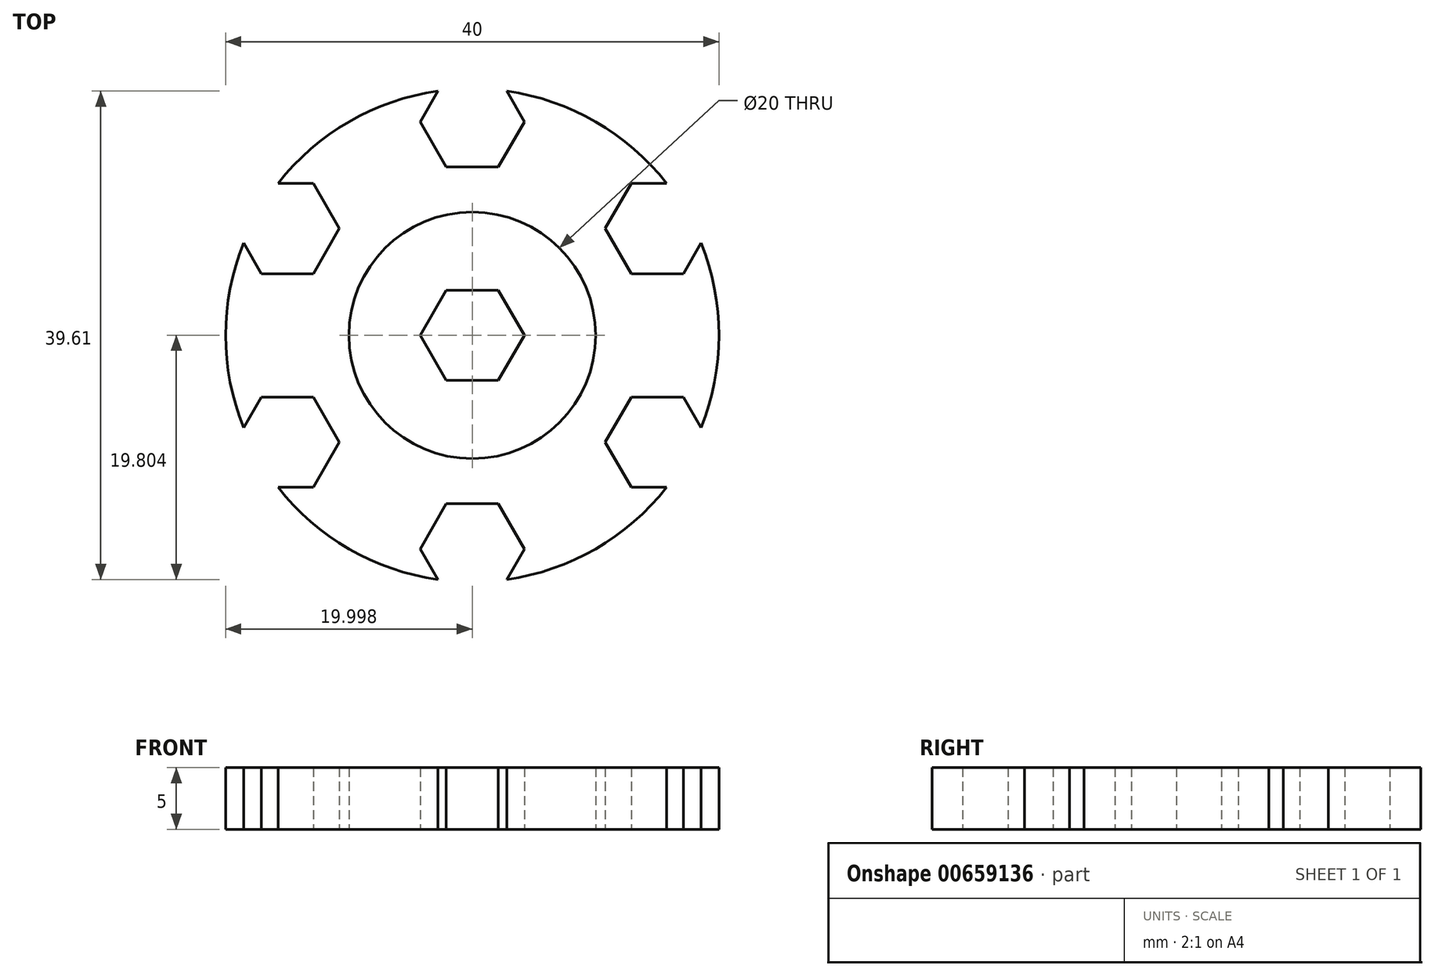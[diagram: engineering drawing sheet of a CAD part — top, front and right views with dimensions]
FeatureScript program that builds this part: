
annotation { "Feature Type Name" : "Feature", "Feature Type Description" : "" }
export const myFeature = defineFeature(function(context is Context, id is Id, definition is map)
    precondition{}
    {
        {
            var Q0;
            Q0=qCreatedBy(makeId("Top.planeOp"),FACE);
            var sketch = newSketch(context, id + "F0", { "sketchPlane" : qUnion([Q0])});
            skLineSegment(sketch, "E0.0", {"start": v(-11.35, 1.25) * mm, "end": v(-21.35, 1.25) * mm});
            skLineSegment(sketch, "E0.1", {"start": v(-21.35, 1.25) * mm, "end": v(-26.35, 9.91) * mm});
            skLineSegment(sketch, "E0.2", {"start": v(-26.35, 9.91) * mm, "end": v(-21.35, 18.57) * mm});
            skLineSegment(sketch, "E0.3", {"start": v(-21.35, 18.57) * mm, "end": v(-11.35, 18.57) * mm});
            skLineSegment(sketch, "E0.4", {"start": v(-11.35, 18.57) * mm, "end": v(-6.35, 9.91) * mm});
            skLineSegment(sketch, "E0.5", {"start": v(-6.35, 9.91) * mm, "end": v(-11.35, 1.25) * mm});
            skPoint(sketch, "E0.0.midPoint", {"position": v(-16.35, 1.25) * mm});
            skLineSegment(sketch, "E1", {"start": v(-21.35, 1.25) * mm, "end": v(-11.35, 1.25) * mm});
            skLineSegment(sketch, "E2", {"start": v(-11.35, 1.25) * mm, "end": v(-6.35, 9.91) * mm});
            skLineSegment(sketch, "E3", {"start": v(-6.35, 9.91) * mm, "end": v(-11.35, 18.57) * mm});
            skLineSegment(sketch, "E4", {"start": v(-11.35, 18.57) * mm, "end": v(-21.35, 18.57) * mm});
            skLineSegment(sketch, "E5", {"start": v(-21.35, 18.57) * mm, "end": v(-26.35, 9.91) * mm});
            skLineSegment(sketch, "E6", {"start": v(-26.35, 9.91) * mm, "end": v(-21.35, 1.25) * mm});
            skLineSegment(sketch, "E7.MirrorCS", {"start": v(-6.35, 27.23) * mm, "end": v(-11.35, 35.9) * mm});
            skLineSegment(sketch, "E8.MirrorCS", {"start": v(-21.35, 35.9) * mm, "end": v(-26.35, 27.23) * mm});
            skLineSegment(sketch, "E9.MirrorCS", {"start": v(-26.35, 27.23) * mm, "end": v(-21.35, 18.57) * mm});
            skLineSegment(sketch, "E10.MirrorCS", {"start": v(-11.35, 35.9) * mm, "end": v(-6.35, 27.23) * mm});
            skLineSegment(sketch, "E11.MirrorCS", {"start": v(-11.35, 35.9) * mm, "end": v(-21.35, 35.9) * mm});
            skLineSegment(sketch, "E12.MirrorCS", {"start": v(-11.35, 18.57) * mm, "end": v(-6.35, 27.23) * mm});
            skLineSegment(sketch, "E13.MirrorCS", {"start": v(-21.35, 35.9) * mm, "end": v(-11.35, 35.9) * mm});
            skLineSegment(sketch, "E14.MirrorCS", {"start": v(-6.35, 27.23) * mm, "end": v(-11.35, 18.57) * mm});
            skLineSegment(sketch, "E15.MirrorCS", {"start": v(-26.35, 27.23) * mm, "end": v(-21.35, 35.9) * mm});
            skLineSegment(sketch, "E16.MirrorCS", {"start": v(-21.35, 18.57) * mm, "end": v(-26.35, 27.23) * mm});
            skPoint(sketch, "E17.MirrorP", {"position": v(-16.35, 35.9) * mm});
            skLineSegment(sketch, "E18.MirrorCS", {"start": v(-6.35, 9.91) * mm, "end": v(3.65, 9.91) * mm});
            skLineSegment(sketch, "E19.MirrorCS", {"start": v(3.65, 9.91) * mm, "end": v(8.65, 18.57) * mm});
            skLineSegment(sketch, "E20.MirrorCS", {"start": v(8.65, 18.57) * mm, "end": v(3.65, 27.23) * mm});
            skLineSegment(sketch, "E21.MirrorCS", {"start": v(3.65, 27.23) * mm, "end": v(-6.35, 27.23) * mm});
            skLineSegment(sketch, "E22.MirrorCS", {"start": v(3.65, 9.91) * mm, "end": v(-6.35, 9.91) * mm});
            skPoint(sketch, "E23.MirrorP", {"position": v(6.15, 14.24) * mm});
            skLineSegment(sketch, "E24.MirrorCS", {"start": v(-6.35, 27.23) * mm, "end": v(3.65, 27.23) * mm});
            skLineSegment(sketch, "E25.MirrorCS", {"start": v(8.65, 18.57) * mm, "end": v(3.65, 9.91) * mm});
            skLineSegment(sketch, "E26.MirrorCS", {"start": v(3.65, 27.23) * mm, "end": v(8.65, 18.57) * mm});
            skLineSegment(sketch, "E27.MirrorCS", {"start": v(8.65, 1.25) * mm, "end": v(3.65, 9.91) * mm});
            skLineSegment(sketch, "E28.MirrorCS", {"start": v(3.65, -7.4) * mm, "end": v(8.65, 1.25) * mm});
            skLineSegment(sketch, "E29.MirrorCS", {"start": v(-6.35, -7.4) * mm, "end": v(3.65, -7.4) * mm});
            skLineSegment(sketch, "E30.MirrorCS", {"start": v(-11.35, 1.25) * mm, "end": v(-6.35, -7.4) * mm});
            skLineSegment(sketch, "E31.MirrorCS", {"start": v(3.65, 9.91) * mm, "end": v(8.65, 1.25) * mm});
            skPoint(sketch, "E32.MirrorP", {"position": v(-8.85, -3.08) * mm});
            skLineSegment(sketch, "E33.MirrorCS", {"start": v(3.65, -7.4) * mm, "end": v(-6.35, -7.4) * mm});
            skLineSegment(sketch, "E34.MirrorCS", {"start": v(-6.35, -7.4) * mm, "end": v(-11.35, 1.25) * mm});
            skLineSegment(sketch, "E35.MirrorCS", {"start": v(8.65, 1.25) * mm, "end": v(3.65, -7.4) * mm});
            skLineSegment(sketch, "E36.MirrorCS", {"start": v(-11.35, -16.07) * mm, "end": v(-6.35, -7.4) * mm});
            skLineSegment(sketch, "E37.MirrorCS", {"start": v(-6.35, -7.4) * mm, "end": v(-11.35, -16.07) * mm});
            skLineSegment(sketch, "E38.MirrorCS", {"start": v(-21.35, -16.07) * mm, "end": v(-11.35, -16.07) * mm});
            skLineSegment(sketch, "E39.MirrorCS", {"start": v(-21.35, 1.25) * mm, "end": v(-26.35, -7.4) * mm});
            skLineSegment(sketch, "E40.MirrorCS", {"start": v(-26.35, -7.4) * mm, "end": v(-21.35, -16.07) * mm});
            skLineSegment(sketch, "E41.MirrorCS", {"start": v(-11.35, -16.07) * mm, "end": v(-21.35, -16.07) * mm});
            skLineSegment(sketch, "E42.MirrorCS", {"start": v(-26.35, -7.4) * mm, "end": v(-21.35, 1.25) * mm});
            skLineSegment(sketch, "E43.MirrorCS", {"start": v(-21.35, -16.07) * mm, "end": v(-26.35, -7.4) * mm});
            skLineSegment(sketch, "E44.MirrorCS", {"start": v(-36.35, -7.4) * mm, "end": v(-26.35, -7.4) * mm});
            skLineSegment(sketch, "E45.MirrorCS", {"start": v(-41.35, 1.25) * mm, "end": v(-36.35, -7.4) * mm});
            skLineSegment(sketch, "E46.MirrorCS", {"start": v(-36.35, -7.4) * mm, "end": v(-41.35, 1.25) * mm});
            skLineSegment(sketch, "E47.MirrorCS", {"start": v(-26.35, -7.4) * mm, "end": v(-36.35, -7.4) * mm});
            skLineSegment(sketch, "E48.MirrorCS", {"start": v(-36.35, 9.91) * mm, "end": v(-41.35, 1.25) * mm});
            skLineSegment(sketch, "E49.MirrorCS", {"start": v(-41.35, 1.25) * mm, "end": v(-36.35, 9.91) * mm});
            skLineSegment(sketch, "E50.MirrorCS", {"start": v(-26.35, 9.91) * mm, "end": v(-36.35, 9.91) * mm});
            skLineSegment(sketch, "E51.MirrorCS", {"start": v(-36.35, 9.91) * mm, "end": v(-26.35, 9.91) * mm});
            skLineSegment(sketch, "E52.MirrorCS", {"start": v(-26.35, 27.23) * mm, "end": v(-36.35, 27.23) * mm});
            skLineSegment(sketch, "E53.MirrorCS", {"start": v(-36.35, 27.23) * mm, "end": v(-41.35, 18.57) * mm});
            skLineSegment(sketch, "E54.MirrorCS", {"start": v(-41.35, 18.57) * mm, "end": v(-36.35, 9.91) * mm});
            skLineSegment(sketch, "E55.MirrorCS", {"start": v(-41.35, 18.57) * mm, "end": v(-36.35, 27.23) * mm});
            skLineSegment(sketch, "E56.MirrorCS", {"start": v(-36.35, 27.23) * mm, "end": v(-26.35, 27.23) * mm});
            skPoint(sketch, "E57.MirrorP", {"position": v(-38.85, 14.24) * mm});
            skLineSegment(sketch, "E58.MirrorCS", {"start": v(-36.35, 9.91) * mm, "end": v(-41.35, 18.57) * mm});
            skLineSegment(sketch, "E59.MirrorCS", {"start": v(-26.35, 44.55) * mm, "end": v(-36.35, 44.55) * mm});
            skLineSegment(sketch, "E60.MirrorCS", {"start": v(-41.35, 35.9) * mm, "end": v(-36.35, 27.23) * mm});
            skLineSegment(sketch, "E61.MirrorCS", {"start": v(-36.35, 44.55) * mm, "end": v(-26.35, 44.55) * mm});
            skLineSegment(sketch, "E62.MirrorCS", {"start": v(-26.35, 44.55) * mm, "end": v(-21.35, 35.9) * mm});
            skLineSegment(sketch, "E63.MirrorCS", {"start": v(-36.35, 44.55) * mm, "end": v(-41.35, 35.9) * mm});
            skLineSegment(sketch, "E64.MirrorCS", {"start": v(-36.35, 27.23) * mm, "end": v(-41.35, 35.9) * mm});
            skLineSegment(sketch, "E65.MirrorCS", {"start": v(-21.35, 35.9) * mm, "end": v(-26.35, 44.55) * mm});
            skPoint(sketch, "E66.MirrorP", {"position": v(-38.85, 40.22) * mm});
            skLineSegment(sketch, "E67.MirrorCS", {"start": v(-41.35, 35.9) * mm, "end": v(-36.35, 44.55) * mm});
            skLineSegment(sketch, "E68.MirrorCS", {"start": v(-56.35, 9.91) * mm, "end": v(-51.35, 18.57) * mm});
            skLineSegment(sketch, "E69.MirrorCS", {"start": v(-41.35, 1.25) * mm, "end": v(-51.35, 1.25) * mm});
            skLineSegment(sketch, "E70.MirrorCS", {"start": v(-56.35, 9.91) * mm, "end": v(-51.35, 1.25) * mm});
            skLineSegment(sketch, "E71.MirrorCS", {"start": v(-51.35, 1.25) * mm, "end": v(-56.35, 9.91) * mm});
            skLineSegment(sketch, "E72.MirrorCS", {"start": v(-51.35, 18.57) * mm, "end": v(-56.35, 9.91) * mm});
            skLineSegment(sketch, "E73.MirrorCS", {"start": v(-51.35, 18.57) * mm, "end": v(-41.35, 18.57) * mm});
            skLineSegment(sketch, "E74.MirrorCS", {"start": v(-41.35, 18.57) * mm, "end": v(-51.35, 18.57) * mm});
            skLineSegment(sketch, "E75.MirrorCS", {"start": v(-51.35, 1.25) * mm, "end": v(-41.35, 1.25) * mm});
            skLineSegment(sketch, "E76.MirrorCS", {"start": v(-6.35, 44.55) * mm, "end": v(3.65, 44.55) * mm});
            skLineSegment(sketch, "E77.MirrorCS", {"start": v(3.65, 44.55) * mm, "end": v(-6.35, 44.55) * mm});
            skLineSegment(sketch, "E78.MirrorCS", {"start": v(8.65, 35.9) * mm, "end": v(3.65, 44.55) * mm});
            skLineSegment(sketch, "E79.MirrorCS", {"start": v(3.65, 44.55) * mm, "end": v(8.65, 35.9) * mm});
            skLineSegment(sketch, "E80.MirrorCS", {"start": v(8.65, 35.9) * mm, "end": v(3.65, 27.23) * mm});
            skLineSegment(sketch, "E81.MirrorCS", {"start": v(3.65, 27.23) * mm, "end": v(8.65, 35.9) * mm});
            skLineSegment(sketch, "E82.MirrorCS", {"start": v(-6.35, 44.55) * mm, "end": v(-11.35, 35.9) * mm});
            skLineSegment(sketch, "E83.MirrorCS", {"start": v(-11.35, 35.9) * mm, "end": v(-6.35, 44.55) * mm});
            skPoint(sketch, "E84.MirrorP", {"position": v(-8.85, 40.22) * mm});
            skLineSegment(sketch, "E85.MirrorCS", {"start": v(23.65, 9.91) * mm, "end": v(18.65, 18.57) * mm});
            skLineSegment(sketch, "E86.MirrorCS", {"start": v(18.65, 1.25) * mm, "end": v(23.65, 9.91) * mm});
            skLineSegment(sketch, "E87.MirrorCS", {"start": v(18.65, 18.57) * mm, "end": v(23.65, 9.91) * mm});
            skLineSegment(sketch, "E88.MirrorCS", {"start": v(23.65, 9.91) * mm, "end": v(18.65, 1.25) * mm});
            skLineSegment(sketch, "E89.MirrorCS", {"start": v(18.65, 1.25) * mm, "end": v(8.65, 1.25) * mm});
            skLineSegment(sketch, "E90.MirrorCS", {"start": v(18.65, 18.57) * mm, "end": v(8.65, 18.57) * mm});
            skLineSegment(sketch, "E91.MirrorCS", {"start": v(8.65, 1.25) * mm, "end": v(18.65, 1.25) * mm});
            skLineSegment(sketch, "E92.MirrorCS", {"start": v(8.65, 18.57) * mm, "end": v(18.65, 18.57) * mm});
            skLineSegment(sketch, "E93.MirrorCS", {"start": v(8.65, -16.07) * mm, "end": v(3.65, -24.73) * mm});
            skLineSegment(sketch, "E94.MirrorCS", {"start": v(3.65, -24.73) * mm, "end": v(8.65, -16.07) * mm});
            skLineSegment(sketch, "E95.MirrorCS", {"start": v(3.65, -24.73) * mm, "end": v(-6.35, -24.73) * mm});
            skLineSegment(sketch, "E96.MirrorCS", {"start": v(-6.35, -24.73) * mm, "end": v(3.65, -24.73) * mm});
            skLineSegment(sketch, "E97.MirrorCS", {"start": v(-6.35, -24.73) * mm, "end": v(-11.35, -16.07) * mm});
            skLineSegment(sketch, "E98.MirrorCS", {"start": v(-11.35, -16.07) * mm, "end": v(-6.35, -24.73) * mm});
            skPoint(sketch, "E99.MirrorP", {"position": v(-16.35, -16.07) * mm});
            skLineSegment(sketch, "E100.MirrorCS", {"start": v(8.65, -16.07) * mm, "end": v(3.65, -7.4) * mm});
            skPoint(sketch, "E101.MirrorP", {"position": v(-8.85, -11.74) * mm});
            skLineSegment(sketch, "E102.MirrorCS", {"start": v(3.65, -7.4) * mm, "end": v(8.65, -16.07) * mm});
            skLineSegment(sketch, "E103.MirrorCS", {"start": v(-26.35, -24.73) * mm, "end": v(-36.35, -24.73) * mm});
            skLineSegment(sketch, "E104.MirrorCS", {"start": v(-36.35, -24.73) * mm, "end": v(-26.35, -24.73) * mm});
            skLineSegment(sketch, "E105.MirrorCS", {"start": v(-36.35, -24.73) * mm, "end": v(-41.35, -16.07) * mm});
            skLineSegment(sketch, "E106.MirrorCS", {"start": v(-41.35, -16.07) * mm, "end": v(-36.35, -24.73) * mm});
            skLineSegment(sketch, "E107.MirrorCS", {"start": v(-41.35, -16.07) * mm, "end": v(-36.35, -7.4) * mm});
            skLineSegment(sketch, "E108.MirrorCS", {"start": v(-26.35, -24.73) * mm, "end": v(-21.35, -16.07) * mm});
            skPoint(sketch, "E109.MirrorP", {"position": v(-38.85, -11.74) * mm});
            skLineSegment(sketch, "E110.MirrorCS", {"start": v(-21.35, -16.07) * mm, "end": v(-26.35, -24.73) * mm});
            skPoint(sketch, "E111.MirrorP", {"position": v(-23.85, -20.4) * mm});
            skLineSegment(sketch, "E112.MirrorCS", {"start": v(-36.35, -7.4) * mm, "end": v(-41.35, -16.07) * mm});
            skPoint(sketch, "E113.MirrorP", {"position": v(-38.85, -20.4) * mm});
            skPoint(sketch, "E114.MirrorP", {"position": v(-31.35, -24.73) * mm});
            skLineSegment(sketch, "E115.0", {"start": v(107.66, 12.57) * mm, "end": v(97.66, 12.57) * mm});
            skLineSegment(sketch, "E115.1", {"start": v(97.66, 12.57) * mm, "end": v(91.43, 20.38) * mm});
            skLineSegment(sketch, "E115.2", {"start": v(91.43, 20.38) * mm, "end": v(93.66, 30.13) * mm});
            skLineSegment(sketch, "E115.3", {"start": v(93.66, 30.13) * mm, "end": v(102.66, 34.47) * mm});
            skLineSegment(sketch, "E115.4", {"start": v(102.66, 34.47) * mm, "end": v(111.67, 30.13) * mm});
            skLineSegment(sketch, "E115.5", {"start": v(111.67, 30.13) * mm, "end": v(113.9, 20.38) * mm});
            skLineSegment(sketch, "E115.6", {"start": v(113.9, 20.38) * mm, "end": v(107.66, 12.57) * mm});
            skPoint(sketch, "E115.0.midPoint", {"position": v(102.66, 12.57) * mm});
            skLineSegment(sketch, "E116", {"start": v(97.66, 12.57) * mm, "end": v(107.66, 12.57) * mm});
            skLineSegment(sketch, "E117", {"start": v(107.66, 12.57) * mm, "end": v(113.9, 20.38) * mm});
            skLineSegment(sketch, "E118", {"start": v(113.9, 20.38) * mm, "end": v(111.67, 30.13) * mm});
            skLineSegment(sketch, "E119", {"start": v(111.67, 30.13) * mm, "end": v(102.66, 34.47) * mm});
            skLineSegment(sketch, "E120", {"start": v(102.66, 34.47) * mm, "end": v(93.66, 30.13) * mm});
            skLineSegment(sketch, "E121", {"start": v(93.66, 30.13) * mm, "end": v(91.43, 20.38) * mm});
            skLineSegment(sketch, "E122", {"start": v(91.43, 20.38) * mm, "end": v(97.66, 12.57) * mm});
            skLineSegment(sketch, "E123.MirrorCS", {"start": v(106.67, 52.04) * mm, "end": v(116.67, 52.04) * mm});
            skLineSegment(sketch, "E124.MirrorCS", {"start": v(100.44, 44.22) * mm, "end": v(106.67, 52.04) * mm});
            skLineSegment(sketch, "E125.MirrorCS", {"start": v(116.67, 52.04) * mm, "end": v(122.9, 44.22) * mm});
            skLineSegment(sketch, "E126.MirrorCS", {"start": v(120.68, 34.47) * mm, "end": v(111.67, 30.13) * mm});
            skLineSegment(sketch, "E127.MirrorCS", {"start": v(122.9, 44.22) * mm, "end": v(120.68, 34.47) * mm});
            skLineSegment(sketch, "E128.MirrorCS", {"start": v(102.66, 34.47) * mm, "end": v(100.44, 44.22) * mm});
            skLineSegment(sketch, "E129.MirrorCS", {"start": v(116.67, 52.04) * mm, "end": v(106.67, 52.04) * mm});
            skLineSegment(sketch, "E130.MirrorCS", {"start": v(106.67, 52.04) * mm, "end": v(100.44, 44.22) * mm});
            skLineSegment(sketch, "E131.MirrorCS", {"start": v(100.44, 44.22) * mm, "end": v(102.66, 34.47) * mm});
            skLineSegment(sketch, "E132.MirrorCS", {"start": v(111.67, 30.13) * mm, "end": v(120.68, 34.47) * mm});
            skLineSegment(sketch, "E133.MirrorCS", {"start": v(122.9, 44.22) * mm, "end": v(116.67, 52.04) * mm});
            skLineSegment(sketch, "E134.MirrorCS", {"start": v(120.68, 34.47) * mm, "end": v(122.9, 44.22) * mm});
            skPoint(sketch, "E135.MirrorP", {"position": v(119.8, 48.13) * mm});
            skLineSegment(sketch, "E136.MirrorCS", {"start": v(111.67, 30.13) * mm, "end": v(117.9, 37.95) * mm});
            skLineSegment(sketch, "E137.MirrorCS", {"start": v(131.92, 20.38) * mm, "end": v(122.9, 16.05) * mm});
            skLineSegment(sketch, "E138.MirrorCS", {"start": v(134.14, 30.13) * mm, "end": v(131.92, 20.38) * mm});
            skLineSegment(sketch, "E139.MirrorCS", {"start": v(127.9, 37.95) * mm, "end": v(134.14, 30.13) * mm});
            skLineSegment(sketch, "E140.MirrorCS", {"start": v(122.9, 16.05) * mm, "end": v(113.9, 20.38) * mm});
            skLineSegment(sketch, "E141.MirrorCS", {"start": v(117.9, 37.95) * mm, "end": v(127.9, 37.95) * mm});
            skLineSegment(sketch, "E142.MirrorCS", {"start": v(131.92, 20.38) * mm, "end": v(134.14, 30.13) * mm});
            skLineSegment(sketch, "E143.MirrorCS", {"start": v(134.14, 30.13) * mm, "end": v(127.9, 37.95) * mm});
            skLineSegment(sketch, "E144.MirrorCS", {"start": v(127.9, 37.95) * mm, "end": v(117.9, 37.95) * mm});
            skPoint(sketch, "E145.MirrorP", {"position": v(127.41, 18.21) * mm});
            skLineSegment(sketch, "E146.MirrorCS", {"start": v(117.9, 37.95) * mm, "end": v(111.67, 30.13) * mm});
            skLineSegment(sketch, "E147.MirrorCS", {"start": v(113.9, 20.38) * mm, "end": v(122.9, 16.05) * mm});
            skLineSegment(sketch, "E148.MirrorCS", {"start": v(122.9, 16.05) * mm, "end": v(131.92, 20.38) * mm});
            skLineSegment(sketch, "E149.MirrorCS", {"start": v(123.9, 20.38) * mm, "end": v(130.13, 12.57) * mm});
            skLineSegment(sketch, "E150.MirrorCS", {"start": v(113.9, 20.38) * mm, "end": v(123.9, 20.38) * mm});
            skLineSegment(sketch, "E151.MirrorCS", {"start": v(127.9, 2.82) * mm, "end": v(118.9, -1.52) * mm});
            skLineSegment(sketch, "E152.MirrorCS", {"start": v(130.13, 12.57) * mm, "end": v(127.9, 2.82) * mm});
            skLineSegment(sketch, "E153.MirrorCS", {"start": v(109.89, 2.82) * mm, "end": v(107.66, 12.57) * mm});
            skLineSegment(sketch, "E154.MirrorCS", {"start": v(118.9, -1.52) * mm, "end": v(109.89, 2.82) * mm});
            skLineSegment(sketch, "E155.MirrorCS", {"start": v(107.66, 12.57) * mm, "end": v(109.89, 2.82) * mm});
            skPoint(sketch, "E156.MirrorP", {"position": v(108.78, 7.7) * mm});
            skLineSegment(sketch, "E157.MirrorCS", {"start": v(123.9, 20.38) * mm, "end": v(113.9, 20.38) * mm});
            skLineSegment(sketch, "E158.MirrorCS", {"start": v(127.9, 2.82) * mm, "end": v(130.13, 12.57) * mm});
            skLineSegment(sketch, "E159.MirrorCS", {"start": v(109.89, 2.82) * mm, "end": v(118.9, -1.52) * mm});
            skLineSegment(sketch, "E160.MirrorCS", {"start": v(130.13, 12.57) * mm, "end": v(123.9, 20.38) * mm});
            skLineSegment(sketch, "E161.MirrorCS", {"start": v(118.9, -1.52) * mm, "end": v(127.9, 2.82) * mm});
            skLineSegment(sketch, "E162.MirrorCS", {"start": v(107.66, 12.57) * mm, "end": v(113.9, 4.75) * mm});
            skLineSegment(sketch, "E163.MirrorCS", {"start": v(111.67, -5) * mm, "end": v(102.66, -9.34) * mm});
            skLineSegment(sketch, "E164.MirrorCS", {"start": v(113.9, 4.75) * mm, "end": v(111.67, -5) * mm});
            skLineSegment(sketch, "E165.MirrorCS", {"start": v(91.43, 4.75) * mm, "end": v(97.66, 12.57) * mm});
            skLineSegment(sketch, "E166.MirrorCS", {"start": v(93.66, -5) * mm, "end": v(91.43, 4.75) * mm});
            skLineSegment(sketch, "E167.MirrorCS", {"start": v(102.66, -9.34) * mm, "end": v(93.66, -5) * mm});
            skLineSegment(sketch, "E168.MirrorCS", {"start": v(97.66, 12.57) * mm, "end": v(91.43, 4.75) * mm});
            skLineSegment(sketch, "E169.MirrorCS", {"start": v(91.43, 4.75) * mm, "end": v(93.66, -5) * mm});
            skLineSegment(sketch, "E170.MirrorCS", {"start": v(93.66, -5) * mm, "end": v(102.66, -9.34) * mm});
            skLineSegment(sketch, "E171.MirrorCS", {"start": v(102.66, -9.34) * mm, "end": v(111.67, -5) * mm});
            skLineSegment(sketch, "E172.MirrorCS", {"start": v(111.67, -5) * mm, "end": v(113.9, 4.75) * mm});
            skLineSegment(sketch, "E173.MirrorCS", {"start": v(113.9, 4.75) * mm, "end": v(107.66, 12.57) * mm});
            skLineSegment(sketch, "E174.MirrorCS", {"start": v(97.66, 12.57) * mm, "end": v(95.44, 2.82) * mm});
            skLineSegment(sketch, "E175.MirrorCS", {"start": v(77.42, 2.82) * mm, "end": v(75.2, 12.57) * mm});
            skLineSegment(sketch, "E176.MirrorCS", {"start": v(86.43, -1.52) * mm, "end": v(77.42, 2.82) * mm});
            skLineSegment(sketch, "E177.MirrorCS", {"start": v(95.44, 2.82) * mm, "end": v(86.43, -1.52) * mm});
            skLineSegment(sketch, "E178.MirrorCS", {"start": v(81.43, 20.38) * mm, "end": v(91.43, 20.38) * mm});
            skLineSegment(sketch, "E179.MirrorCS", {"start": v(75.2, 12.57) * mm, "end": v(81.43, 20.38) * mm});
            skPoint(sketch, "E180.MirrorP", {"position": v(96.55, 7.7) * mm});
            skLineSegment(sketch, "E181.MirrorCS", {"start": v(86.43, -1.52) * mm, "end": v(95.44, 2.82) * mm});
            skLineSegment(sketch, "E182.MirrorCS", {"start": v(77.42, 2.82) * mm, "end": v(86.43, -1.52) * mm});
            skLineSegment(sketch, "E183.MirrorCS", {"start": v(95.44, 2.82) * mm, "end": v(97.66, 12.57) * mm});
            skLineSegment(sketch, "E184.MirrorCS", {"start": v(75.2, 12.57) * mm, "end": v(77.42, 2.82) * mm});
            skLineSegment(sketch, "E185.MirrorCS", {"start": v(81.43, 20.38) * mm, "end": v(75.2, 12.57) * mm});
            skLineSegment(sketch, "E186.MirrorCS", {"start": v(91.43, 20.38) * mm, "end": v(81.43, 20.38) * mm});
            skLineSegment(sketch, "E187.MirrorCS", {"start": v(82.42, 44.22) * mm, "end": v(88.66, 52.04) * mm});
            skLineSegment(sketch, "E188.MirrorCS", {"start": v(88.66, 52.04) * mm, "end": v(98.66, 52.04) * mm});
            skLineSegment(sketch, "E189.MirrorCS", {"start": v(84.65, 34.47) * mm, "end": v(82.42, 44.22) * mm});
            skLineSegment(sketch, "E190.MirrorCS", {"start": v(104.89, 44.22) * mm, "end": v(102.66, 34.47) * mm});
            skLineSegment(sketch, "E191.MirrorCS", {"start": v(98.66, 52.04) * mm, "end": v(104.89, 44.22) * mm});
            skLineSegment(sketch, "E192.MirrorCS", {"start": v(82.42, 44.22) * mm, "end": v(84.65, 34.47) * mm});
            skPoint(sketch, "E193.MirrorP", {"position": v(85.54, 48.13) * mm});
            skLineSegment(sketch, "E194.MirrorCS", {"start": v(93.66, 30.13) * mm, "end": v(84.65, 34.47) * mm});
            skLineSegment(sketch, "E195.MirrorCS", {"start": v(98.66, 52.04) * mm, "end": v(88.66, 52.04) * mm});
            skLineSegment(sketch, "E196.MirrorCS", {"start": v(84.65, 34.47) * mm, "end": v(93.66, 30.13) * mm});
            skLineSegment(sketch, "E197.MirrorCS", {"start": v(104.89, 44.22) * mm, "end": v(98.66, 52.04) * mm});
            skLineSegment(sketch, "E198.MirrorCS", {"start": v(102.66, 34.47) * mm, "end": v(104.89, 44.22) * mm});
            skLineSegment(sketch, "E199.MirrorCS", {"start": v(88.66, 52.04) * mm, "end": v(82.42, 44.22) * mm});
            skLineSegment(sketch, "E200.MirrorCS", {"start": v(82.42, 16.05) * mm, "end": v(73.41, 20.38) * mm});
            skLineSegment(sketch, "E201.MirrorCS", {"start": v(73.41, 20.38) * mm, "end": v(82.42, 16.05) * mm});
            skLineSegment(sketch, "E202.MirrorCS", {"start": v(87.42, 37.95) * mm, "end": v(93.66, 30.13) * mm});
            skLineSegment(sketch, "E203.MirrorCS", {"start": v(77.42, 37.95) * mm, "end": v(87.42, 37.95) * mm});
            skLineSegment(sketch, "E204.MirrorCS", {"start": v(71.19, 30.13) * mm, "end": v(77.42, 37.95) * mm});
            skLineSegment(sketch, "E205.MirrorCS", {"start": v(73.41, 20.38) * mm, "end": v(71.19, 30.13) * mm});
            skLineSegment(sketch, "E206.MirrorCS", {"start": v(91.43, 20.38) * mm, "end": v(82.42, 16.05) * mm});
            skLineSegment(sketch, "E207.MirrorCS", {"start": v(82.42, 16.05) * mm, "end": v(91.43, 20.38) * mm});
            skPoint(sketch, "E208.MirrorP", {"position": v(77.92, 18.21) * mm});
            skLineSegment(sketch, "E209.MirrorCS", {"start": v(93.66, 30.13) * mm, "end": v(87.42, 37.95) * mm});
            skLineSegment(sketch, "E210.MirrorCS", {"start": v(71.19, 30.13) * mm, "end": v(73.41, 20.38) * mm});
            skLineSegment(sketch, "E211.MirrorCS", {"start": v(77.42, 37.95) * mm, "end": v(71.19, 30.13) * mm});
            skLineSegment(sketch, "E212.MirrorCS", {"start": v(87.42, 37.95) * mm, "end": v(77.42, 37.95) * mm});
            skCircle(sketch, "E213", {"center": v(67.92, -62.3) * mm, "radius": 40 * mm});
            skLineSegment(sketch, "E214", {"start": v(-11.35, 18.57) * mm, "end": v(-21.35, 1.25) * mm});
            skLineSegment(sketch, "E215", {"start": v(-26.35, 9.91) * mm, "end": v(-6.35, 9.91) * mm});
            skLineSegment(sketch, "E216", {"start": v(-11.35, 1.25) * mm, "end": v(-21.35, 18.57) * mm});
            skPoint(sketch, "E217", {"position": v(-16.35, 9.91) * mm});
            skCircle(sketch, "E218", {"center": v(-16.35, 9.91) * mm, "radius": 15 * mm});
            skPoint(sketch, "E219", {"position": v(-31.35, 9.91) * mm});
            skPoint(sketch, "E220", {"position": v(-1.35, 9.91) * mm});
            skPoint(sketch, "E221", {"position": v(-23.85, -3.08) * mm});
            skPoint(sketch, "E222", {"position": v(-23.85, 22.9) * mm});
            skPoint(sketch, "E223", {"position": v(-8.85, 22.9) * mm});
            skLineSegment(sketch, "E224.0", {"start": v(-3.47, 39.55) * mm, "end": v(0.76, 39.55) * mm});
            skLineSegment(sketch, "E224.1", {"start": v(2.87, 35.9) * mm, "end": v(0.76, 32.23) * mm});
            skLineSegment(sketch, "E224.2", {"start": v(0.76, 32.23) * mm, "end": v(-3.47, 32.23) * mm});
            skLineSegment(sketch, "E224.3", {"start": v(0.76, 39.55) * mm, "end": v(2.87, 35.9) * mm});
            skLineSegment(sketch, "E224.4", {"start": v(-3.47, 32.23) * mm, "end": v(-5.58, 35.9) * mm});
            skLineSegment(sketch, "E224.5", {"start": v(-5.58, 35.9) * mm, "end": v(-3.47, 39.55) * mm});
            skLineSegment(sketch, "E225.0", {"start": v(0.76, 22.23) * mm, "end": v(-3.47, 22.23) * mm});
            skLineSegment(sketch, "E225.1", {"start": v(2.87, 18.57) * mm, "end": v(0.76, 14.91) * mm});
            skLineSegment(sketch, "E225.2", {"start": v(-3.47, 14.91) * mm, "end": v(0.76, 14.91) * mm});
            skLineSegment(sketch, "E225.3", {"start": v(0.76, 22.23) * mm, "end": v(2.87, 18.57) * mm});
            skLineSegment(sketch, "E225.4", {"start": v(-3.47, 14.91) * mm, "end": v(-5.58, 18.57) * mm});
            skLineSegment(sketch, "E225.5", {"start": v(-5.58, 18.57) * mm, "end": v(-3.47, 22.23) * mm});
            skLineSegment(sketch, "E226.0", {"start": v(-18.47, 30.9) * mm, "end": v(-20.58, 27.23) * mm});
            skLineSegment(sketch, "E226.1", {"start": v(-12.13, 27.23) * mm, "end": v(-14.24, 30.9) * mm});
            skLineSegment(sketch, "E226.2", {"start": v(-14.24, 23.57) * mm, "end": v(-12.13, 27.23) * mm});
            skLineSegment(sketch, "E226.3", {"start": v(-18.47, 30.9) * mm, "end": v(-14.24, 30.9) * mm});
            skLineSegment(sketch, "E226.4", {"start": v(-14.24, 23.57) * mm, "end": v(-18.47, 23.57) * mm});
            skLineSegment(sketch, "E226.5", {"start": v(-20.58, 27.23) * mm, "end": v(-18.47, 23.57) * mm});
            skLineSegment(sketch, "E227.0", {"start": v(-29.24, 39.55) * mm, "end": v(-27.13, 35.9) * mm});
            skLineSegment(sketch, "E227.1", {"start": v(-33.47, 32.23) * mm, "end": v(-29.24, 32.23) * mm});
            skLineSegment(sketch, "E227.2", {"start": v(-35.58, 35.9) * mm, "end": v(-33.47, 32.23) * mm});
            skLineSegment(sketch, "E227.3", {"start": v(-27.13, 35.9) * mm, "end": v(-29.24, 32.23) * mm});
            skLineSegment(sketch, "E227.4", {"start": v(-35.58, 35.9) * mm, "end": v(-33.47, 39.55) * mm});
            skLineSegment(sketch, "E227.5", {"start": v(-33.47, 39.55) * mm, "end": v(-29.24, 39.55) * mm});
            skLineSegment(sketch, "E228.0", {"start": v(17.87, 9.91) * mm, "end": v(15.76, 13.57) * mm});
            skLineSegment(sketch, "E228.1", {"start": v(11.53, 13.57) * mm, "end": v(9.42, 9.91) * mm});
            skLineSegment(sketch, "E228.2", {"start": v(9.42, 9.91) * mm, "end": v(11.53, 6.25) * mm});
            skLineSegment(sketch, "E228.3", {"start": v(15.76, 13.57) * mm, "end": v(11.53, 13.57) * mm});
            skLineSegment(sketch, "E228.4", {"start": v(11.53, 6.25) * mm, "end": v(15.76, 6.25) * mm});
            skLineSegment(sketch, "E228.5", {"start": v(15.76, 6.25) * mm, "end": v(17.87, 9.91) * mm});
            skCircle(sketch, "E229.0", {"center": v(-16.35, 9.91) * mm, "radius": 20 * mm});
            skCircle(sketch, "E230.0", {"center": v(-16.35, 9.91) * mm, "radius": 10 * mm});
            skLineSegment(sketch, "E231.0", {"start": v(-35.58, 18.57) * mm, "end": v(-33.47, 22.23) * mm});
            skLineSegment(sketch, "E231.1", {"start": v(-29.24, 22.23) * mm, "end": v(-27.13, 18.57) * mm});
            skLineSegment(sketch, "E231.2", {"start": v(-27.13, 18.57) * mm, "end": v(-29.24, 14.91) * mm});
            skLineSegment(sketch, "E231.3", {"start": v(-33.47, 22.23) * mm, "end": v(-29.24, 22.23) * mm});
            skLineSegment(sketch, "E231.4", {"start": v(-29.24, 14.91) * mm, "end": v(-33.47, 14.91) * mm});
            skLineSegment(sketch, "E231.5", {"start": v(-33.47, 14.91) * mm, "end": v(-35.58, 18.57) * mm});
            skLineSegment(sketch, "E232.0", {"start": v(-5.58, 1.25) * mm, "end": v(-3.47, 4.91) * mm});
            skLineSegment(sketch, "E232.1", {"start": v(0.76, 4.91) * mm, "end": v(2.87, 1.25) * mm});
            skLineSegment(sketch, "E232.2", {"start": v(2.87, 1.25) * mm, "end": v(0.76, -2.4) * mm});
            skLineSegment(sketch, "E232.3", {"start": v(-3.47, 4.91) * mm, "end": v(0.76, 4.91) * mm});
            skLineSegment(sketch, "E232.4", {"start": v(0.76, -2.4) * mm, "end": v(-3.47, -2.4) * mm});
            skLineSegment(sketch, "E232.5", {"start": v(-5.58, 1.25) * mm, "end": v(-3.47, -2.4) * mm});
            skLineSegment(sketch, "E233.0", {"start": v(-12.13, 9.91) * mm, "end": v(-14.24, 13.57) * mm});
            skLineSegment(sketch, "E233.1", {"start": v(-18.47, 13.57) * mm, "end": v(-20.58, 9.91) * mm});
            skLineSegment(sketch, "E233.2", {"start": v(-20.58, 9.91) * mm, "end": v(-18.47, 6.25) * mm});
            skLineSegment(sketch, "E233.3", {"start": v(-14.24, 13.57) * mm, "end": v(-18.47, 13.57) * mm});
            skLineSegment(sketch, "E233.4", {"start": v(-18.47, 6.25) * mm, "end": v(-14.24, 6.25) * mm});
            skLineSegment(sketch, "E233.5", {"start": v(-14.24, 6.25) * mm, "end": v(-12.13, 9.91) * mm});
            skLineSegment(sketch, "E234.0", {"start": v(-29.24, 4.91) * mm, "end": v(-27.13, 1.25) * mm});
            skLineSegment(sketch, "E234.1", {"start": v(-33.47, 4.91) * mm, "end": v(-35.58, 1.25) * mm});
            skLineSegment(sketch, "E234.2", {"start": v(-35.58, 1.25) * mm, "end": v(-33.47, -2.4) * mm});
            skLineSegment(sketch, "E234.3", {"start": v(-29.24, 4.91) * mm, "end": v(-33.47, 4.91) * mm});
            skLineSegment(sketch, "E234.4", {"start": v(-33.47, -2.4) * mm, "end": v(-29.24, -2.4) * mm});
            skLineSegment(sketch, "E234.5", {"start": v(-29.24, -2.4) * mm, "end": v(-27.13, 1.25) * mm});
            skLineSegment(sketch, "E235.0", {"start": v(-48.47, 13.57) * mm, "end": v(-50.58, 9.91) * mm});
            skLineSegment(sketch, "E235.1", {"start": v(-42.13, 9.91) * mm, "end": v(-44.24, 13.57) * mm});
            skLineSegment(sketch, "E235.2", {"start": v(-42.13, 9.91) * mm, "end": v(-44.24, 6.25) * mm});
            skLineSegment(sketch, "E235.3", {"start": v(-48.47, 13.57) * mm, "end": v(-44.24, 13.57) * mm});
            skLineSegment(sketch, "E235.4", {"start": v(-44.24, 6.25) * mm, "end": v(-48.47, 6.25) * mm});
            skLineSegment(sketch, "E235.5", {"start": v(-48.47, 6.25) * mm, "end": v(-50.58, 9.91) * mm});
            skLineSegment(sketch, "E236.0", {"start": v(-18.47, -11.07) * mm, "end": v(-20.58, -7.4) * mm});
            skLineSegment(sketch, "E236.1", {"start": v(-14.24, -11.07) * mm, "end": v(-12.13, -7.4) * mm});
            skLineSegment(sketch, "E236.2", {"start": v(-14.24, -3.75) * mm, "end": v(-12.13, -7.4) * mm});
            skLineSegment(sketch, "E236.3", {"start": v(-18.47, -11.07) * mm, "end": v(-14.24, -11.07) * mm});
            skLineSegment(sketch, "E236.4", {"start": v(-18.47, -3.75) * mm, "end": v(-14.24, -3.75) * mm});
            skLineSegment(sketch, "E236.5", {"start": v(-20.58, -7.4) * mm, "end": v(-18.47, -3.75) * mm});
            skLineSegment(sketch, "E237.0", {"start": v(-35.58, -16.07) * mm, "end": v(-33.47, -12.4) * mm});
            skLineSegment(sketch, "E237.1", {"start": v(-27.13, -16.07) * mm, "end": v(-29.24, -12.4) * mm});
            skLineSegment(sketch, "E237.2", {"start": v(-29.24, -19.73) * mm, "end": v(-27.13, -16.07) * mm});
            skLineSegment(sketch, "E237.3", {"start": v(-33.47, -12.4) * mm, "end": v(-29.24, -12.4) * mm});
            skLineSegment(sketch, "E237.4", {"start": v(-29.24, -19.73) * mm, "end": v(-33.47, -19.73) * mm});
            skLineSegment(sketch, "E237.5", {"start": v(-33.47, -19.73) * mm, "end": v(-35.58, -16.07) * mm});
            skLineSegment(sketch, "E238.0", {"start": v(2.87, -16.07) * mm, "end": v(0.76, -12.4) * mm});
            skLineSegment(sketch, "E238.1", {"start": v(-5.58, -16.07) * mm, "end": v(-3.47, -12.4) * mm});
            skLineSegment(sketch, "E238.2", {"start": v(-5.58, -16.07) * mm, "end": v(-3.47, -19.73) * mm});
            skLineSegment(sketch, "E238.3", {"start": v(0.76, -12.4) * mm, "end": v(-3.47, -12.4) * mm});
            skLineSegment(sketch, "E238.4", {"start": v(0.76, -19.73) * mm, "end": v(-3.47, -19.73) * mm});
            skLineSegment(sketch, "E238.5", {"start": v(2.87, -16.07) * mm, "end": v(0.76, -19.73) * mm});
            skSolve(sketch);
        }
        {
            var Q0;
            Q0=makeQuery(id+"F0.imprint","IMPRINT",FACE,{"disambiguationData":[TD([[makeQuery(id+"F0.imprint","IMPRINT",EDGE,{"derivedFrom":sQuery(id+"F0.wireOp",EDGE,"E38.MirrorCS")}),1.0]])]});
            var Q1;
            {var subQ0=sQuery(id+"F0.wireOp",EDGE,"E0.2");Q1=makeQuery(id+"F0.imprint","IMPRINT",FACE,{"disambiguationData":[TD([[makeQuery(id+"F0.imprint","IMPRINT",EDGE,{"derivedFrom":subQ0}),-1.0]])]});}
            var Q2;
            Q2=makeQuery(id+"F0.imprint","IMPRINT",FACE,{"disambiguationData":[TD([[makeQuery(id+"F0.imprint","IMPRINT",EDGE,{"derivedFrom":sQuery(id+"F0.wireOp",EDGE,"E55.MirrorCS")}),-1.0]])]});
            var Q3;
            Q3=makeQuery(id+"F0.imprint","IMPRINT",FACE,{"disambiguationData":[TD([[makeQuery(id+"F0.imprint","IMPRINT",EDGE,{"derivedFrom":sQuery(id+"F0.wireOp",EDGE,"E52.MirrorCS")}),-1.0]])]});
            var Q4;
            Q4=makeQuery(id+"F0.imprint","IMPRINT",FACE,{"disambiguationData":[TD([[makeQuery(id+"F0.imprint","IMPRINT",EDGE,{"derivedFrom":sQuery(id+"F0.wireOp",EDGE,"E49.MirrorCS")}),1.0]])]});
            var Q5;
            {var subQ13=sQuery(id+"F0.wireOp",EDGE,"E225.4");Q5=makeQuery(id+"F0.imprint","IMPRINT",FACE,{"disambiguationData":[TD([[makeQuery(id+"F0.imprint","IMPRINT",EDGE,{"derivedFrom":subQ13}),1.0]])]});}
            var Q6;
            Q6=makeQuery(id+"F0.imprint","IMPRINT",FACE,{"disambiguationData":[TD([[makeQuery(id+"F0.imprint","IMPRINT",EDGE,{"derivedFrom":sQuery(id+"F0.wireOp",EDGE,"E7.MirrorCS")}),-1.0]])]});
            var Q7;
            Q7=makeQuery(id+"F0.imprint","IMPRINT",FACE,{"disambiguationData":[TD([[makeQuery(id+"F0.imprint","IMPRINT",EDGE,{"derivedFrom":sQuery(id+"F0.wireOp",EDGE,"E19.MirrorCS")}),-1.0]])]});
            var Q8;
            {var subQ0=sQuery(id+"F0.wireOp",EDGE,"E0.4");Q8=makeQuery(id+"F0.imprint","IMPRINT",FACE,{"disambiguationData":[TD([[makeQuery(id+"F0.imprint","IMPRINT",EDGE,{"derivedFrom":subQ0}),-1.0]])]});}
            var Q9;
            Q9=makeQuery(id+"F0.imprint","IMPRINT",FACE,{"disambiguationData":[TD([[makeQuery(id+"F0.imprint","IMPRINT",EDGE,{"derivedFrom":sQuery(id+"F0.wireOp",EDGE,"E33.MirrorCS")}),1.0]])]});
            var Q10;
            {var subQ12=sQuery(id+"F0.wireOp",EDGE,"E231.2");Q10=makeQuery(id+"F0.imprint","IMPRINT",FACE,{"disambiguationData":[TD([[makeQuery(id+"F0.imprint","IMPRINT",EDGE,{"derivedFrom":subQ12}),1.0]])]});}
            var Q11;
            Q11=makeQuery(id+"F0.imprint","IMPRINT",FACE,{"disambiguationData":[TD([[makeQuery(id+"F0.imprint","IMPRINT",EDGE,{"derivedFrom":sQuery(id+"F0.wireOp",EDGE,"E104.MirrorCS")}),1.0]])]});
            var Q12;
            Q12=makeQuery(id+"F0.imprint","IMPRINT",FACE,{"disambiguationData":[TD([[makeQuery(id+"F0.imprint","IMPRINT",EDGE,{"derivedFrom":sQuery(id+"F0.wireOp",EDGE,"E45.MirrorCS")}),1.0]])]});
            var Q13;
            Q13=makeQuery(id+"F0.imprint","IMPRINT",FACE,{"disambiguationData":[TD([[makeQuery(id+"F0.imprint","IMPRINT",EDGE,{"derivedFrom":sQuery(id+"F0.wireOp",EDGE,"E26.MirrorCS")}),-1.0]])]});
            var Q14;
            Q14=makeQuery(id+"F0.imprint","IMPRINT",FACE,{"disambiguationData":[TD([[makeQuery(id+"F0.imprint","IMPRINT",EDGE,{"derivedFrom":sQuery(id+"F0.wireOp",EDGE,"E13.MirrorCS")}),-1.0]])]});
            var Q15;
            Q15=makeQuery(id+"F0.imprint","IMPRINT",FACE,{"disambiguationData":[TD([[makeQuery(id+"F0.imprint","IMPRINT",EDGE,{"derivedFrom":sQuery(id+"F0.wireOp",EDGE,"E35.MirrorCS")}),-1.0]])]});
            var Q16;
            {var subQ1=sQuery(id+"F0.wireOp",EDGE,"E16.MirrorCS");var subQ7=sQuery(id+"F0.wireOp",EDGE,"E218");var subQ9=makeQuery(id+"F0.imprint","INTERSECT",VERTEX,{"derivedFrom":[subQ1,subQ7]});Q16=makeQuery(id+"F0.imprint","IMPRINT",FACE,{"disambiguationData":[TD([[makeQuery(id+"F0.imprint","IMPRINT",EDGE,{"disambiguationData":[TD([[subQ9,-1.0]])],"derivedFrom":subQ7}),-1.0]])]});}
            var Q17;
            {var subQ3=sQuery(id+"F0.wireOp",EDGE,"E218");var subQ5=sQuery(id+"F0.wireOp",EDGE,"E51.MirrorCS");var subQ6=makeQuery(id+"F0.imprint","INTERSECT",VERTEX,{"derivedFrom":[subQ5,subQ3]});Q17=makeQuery(id+"F0.imprint","IMPRINT",FACE,{"disambiguationData":[TD([[makeQuery(id+"F0.imprint","IMPRINT",EDGE,{"disambiguationData":[TD([[subQ6,1.0]])],"derivedFrom":subQ3}),-1.0]])]});}
            var Q18;
            {var subQ5=sQuery(id+"F0.wireOp",EDGE,"E232.0");Q18=makeQuery(id+"F0.imprint","IMPRINT",FACE,{"disambiguationData":[TD([[makeQuery(id+"F0.imprint","IMPRINT",EDGE,{"derivedFrom":subQ5}),1.0]])]});}
            var Q19;
            {var subQ5=sQuery(id+"F0.wireOp",EDGE,"E51.MirrorCS");var subQ7=sQuery(id+"F0.wireOp",EDGE,"E218");var subQ8=makeQuery(id+"F0.imprint","INTERSECT",VERTEX,{"derivedFrom":[subQ5,subQ7]});Q19=makeQuery(id+"F0.imprint","IMPRINT",FACE,{"disambiguationData":[TD([[makeQuery(id+"F0.imprint","IMPRINT",EDGE,{"disambiguationData":[TD([[subQ8,-1.0]])],"derivedFrom":subQ7}),-1.0]])]});}
            var Q20;
            {var subQ13=sQuery(id+"F0.wireOp",EDGE,"E236.4");Q20=makeQuery(id+"F0.imprint","IMPRINT",FACE,{"disambiguationData":[TD([[makeQuery(id+"F0.imprint","IMPRINT",EDGE,{"derivedFrom":subQ13}),1.0]])]});}
            var Q21;
            {var subQ5=sQuery(id+"F0.wireOp",EDGE,"E12.MirrorCS");var subQ7=sQuery(id+"F0.wireOp",EDGE,"E218");var subQ8=makeQuery(id+"F0.imprint","INTERSECT",VERTEX,{"derivedFrom":[subQ5,subQ7]});Q21=makeQuery(id+"F0.imprint","IMPRINT",FACE,{"disambiguationData":[TD([[makeQuery(id+"F0.imprint","IMPRINT",EDGE,{"disambiguationData":[TD([[subQ8,1.0]])],"derivedFrom":subQ7}),-1.0]])]});}
            var Q22;
            {var subQ11=sQuery(id+"F0.wireOp",EDGE,"E234.0");Q22=makeQuery(id+"F0.imprint","IMPRINT",FACE,{"disambiguationData":[TD([[makeQuery(id+"F0.imprint","IMPRINT",EDGE,{"derivedFrom":subQ11}),1.0]])]});}
            var Q23;
            {var subQ5=sQuery(id+"F0.wireOp",EDGE,"E226.4");Q23=makeQuery(id+"F0.imprint","IMPRINT",FACE,{"disambiguationData":[TD([[makeQuery(id+"F0.imprint","IMPRINT",EDGE,{"derivedFrom":subQ5}),1.0]])]});}
            var Q24;
            {var subQ5=sQuery(id+"F0.wireOp",EDGE,"E218");var subQ6=sQuery(id+"F0.wireOp",EDGE,"E22.MirrorCS");var subQ7=makeQuery(id+"F0.imprint","INTERSECT",VERTEX,{"derivedFrom":[subQ6,subQ5]});Q24=makeQuery(id+"F0.imprint","IMPRINT",FACE,{"disambiguationData":[TD([[makeQuery(id+"F0.imprint","IMPRINT",EDGE,{"disambiguationData":[TD([[subQ7,-1.0]])],"derivedFrom":subQ5}),-1.0]])]});}
            var Q25;
            {var subQ1=sQuery(id+"F0.wireOp",EDGE,"E42.MirrorCS");var subQ5=sQuery(id+"F0.wireOp",EDGE,"E218");var subQ6=makeQuery(id+"F0.imprint","INTERSECT",VERTEX,{"derivedFrom":[subQ1,subQ5]});Q25=makeQuery(id+"F0.imprint","IMPRINT",FACE,{"disambiguationData":[TD([[makeQuery(id+"F0.imprint","IMPRINT",EDGE,{"disambiguationData":[TD([[subQ6,1.0]])],"derivedFrom":subQ5}),-1.0]])]});}
            var Q26;
            {var subQ5=sQuery(id+"F0.wireOp",EDGE,"E30.MirrorCS");var subQ7=sQuery(id+"F0.wireOp",EDGE,"E218");var subQ8=makeQuery(id+"F0.imprint","INTERSECT",VERTEX,{"derivedFrom":[subQ5,subQ7]});Q26=makeQuery(id+"F0.imprint","IMPRINT",FACE,{"disambiguationData":[TD([[makeQuery(id+"F0.imprint","IMPRINT",EDGE,{"disambiguationData":[TD([[subQ8,-1.0]])],"derivedFrom":subQ7}),-1.0]])]});}
            var Q27;
            {var subQ5=sQuery(id+"F0.wireOp",EDGE,"E22.MirrorCS");var subQ7=sQuery(id+"F0.wireOp",EDGE,"E218");var subQ9=makeQuery(id+"F0.imprint","INTERSECT",VERTEX,{"derivedFrom":[subQ5,subQ7]});Q27=makeQuery(id+"F0.imprint","IMPRINT",FACE,{"disambiguationData":[TD([[makeQuery(id+"F0.imprint","IMPRINT",EDGE,{"disambiguationData":[TD([[subQ9,1.0]])],"derivedFrom":subQ7}),-1.0]])]});}
            var Q28;
            {var subQ0=sQuery(id+"F0.wireOp",EDGE,"E218");var subQ1=sQuery(id+"F0.wireOp",EDGE,"E42.MirrorCS");var subQ2=makeQuery(id+"F0.imprint","INTERSECT",VERTEX,{"derivedFrom":[subQ1,subQ0]});Q28=makeQuery(id+"F0.imprint","IMPRINT",FACE,{"disambiguationData":[TD([[makeQuery(id+"F0.imprint","IMPRINT",EDGE,{"disambiguationData":[TD([[subQ2,-1.0]])],"derivedFrom":subQ0}),-1.0]])]});}
            var Q29;
            {var subQ3=sQuery(id+"F0.wireOp",EDGE,"E218");var subQ7=sQuery(id+"F0.wireOp",EDGE,"E12.MirrorCS");var subQ8=makeQuery(id+"F0.imprint","INTERSECT",VERTEX,{"derivedFrom":[subQ7,subQ3]});Q29=makeQuery(id+"F0.imprint","IMPRINT",FACE,{"disambiguationData":[TD([[makeQuery(id+"F0.imprint","IMPRINT",EDGE,{"disambiguationData":[TD([[subQ8,-1.0]])],"derivedFrom":subQ3}),-1.0]])]});}
            var Q30;
            {var subQ3=sQuery(id+"F0.wireOp",EDGE,"E218");var subQ7=sQuery(id+"F0.wireOp",EDGE,"E16.MirrorCS");var subQ8=makeQuery(id+"F0.imprint","INTERSECT",VERTEX,{"derivedFrom":[subQ7,subQ3]});Q30=makeQuery(id+"F0.imprint","IMPRINT",FACE,{"disambiguationData":[TD([[makeQuery(id+"F0.imprint","IMPRINT",EDGE,{"disambiguationData":[TD([[subQ8,1.0]])],"derivedFrom":subQ3}),-1.0]])]});}
            var Q31;
            {var subQ0=sQuery(id+"F0.wireOp",EDGE,"E0.0");Q31=makeQuery(id+"F0.imprint","IMPRINT",FACE,{"disambiguationData":[TD([[makeQuery(id+"F0.imprint","IMPRINT",EDGE,{"derivedFrom":subQ0}),-1.0]])]});}
            var Q32;
            {var subQ5=sQuery(id+"F0.wireOp",EDGE,"E30.MirrorCS");var subQ7=sQuery(id+"F0.wireOp",EDGE,"E218");var subQ8=makeQuery(id+"F0.imprint","INTERSECT",VERTEX,{"derivedFrom":[subQ5,subQ7]});Q32=makeQuery(id+"F0.imprint","IMPRINT",FACE,{"disambiguationData":[TD([[makeQuery(id+"F0.imprint","IMPRINT",EDGE,{"disambiguationData":[TD([[subQ8,1.0]])],"derivedFrom":subQ7}),-1.0]])]});}
            var Q33;
            {var subQ0=sQuery(id+"F0.wireOp",EDGE,"E233.0");Q33=makeQuery(id+"F0.imprint","IMPRINT",FACE,{"disambiguationData":[TD([[makeQuery(id+"F0.imprint","IMPRINT",EDGE,{"derivedFrom":subQ0}),1.0]])]});}
            var Q34;
            {var subQ0=sQuery(id+"F0.wireOp",EDGE,"E233.3");Q34=makeQuery(id+"F0.imprint","IMPRINT",FACE,{"disambiguationData":[TD([[makeQuery(id+"F0.imprint","IMPRINT",EDGE,{"derivedFrom":subQ0}),1.0]])]});}
            var Q35;
            {var subQ0=sQuery(id+"F0.wireOp",EDGE,"E233.1");Q35=makeQuery(id+"F0.imprint","IMPRINT",FACE,{"disambiguationData":[TD([[makeQuery(id+"F0.imprint","IMPRINT",EDGE,{"derivedFrom":subQ0}),1.0]])]});}
            var Q36;
            {var subQ0=sQuery(id+"F0.wireOp",EDGE,"E233.5");Q36=makeQuery(id+"F0.imprint","IMPRINT",FACE,{"disambiguationData":[TD([[makeQuery(id+"F0.imprint","IMPRINT",EDGE,{"derivedFrom":subQ0}),1.0]])]});}
            var Q37;
            {var subQ0=sQuery(id+"F0.wireOp",EDGE,"E233.2");Q37=makeQuery(id+"F0.imprint","IMPRINT",FACE,{"disambiguationData":[TD([[makeQuery(id+"F0.imprint","IMPRINT",EDGE,{"derivedFrom":subQ0}),1.0]])]});}
            var Q38;
            {var subQ0=sQuery(id+"F0.wireOp",EDGE,"E233.4");Q38=makeQuery(id+"F0.imprint","IMPRINT",FACE,{"disambiguationData":[TD([[makeQuery(id+"F0.imprint","IMPRINT",EDGE,{"derivedFrom":subQ0}),1.0]])]});}
            var Q39;
            {var subQ0=sQuery(id+"F0.wireOp",EDGE,"E0.2");Q39=makeQuery(id+"F0.imprint","IMPRINT",FACE,{"disambiguationData":[TD([[makeQuery(id+"F0.imprint","IMPRINT",EDGE,{"derivedFrom":subQ0}),1.0]])]});}
            var Q40;
            {var subQ0=sQuery(id+"F0.wireOp",EDGE,"E0.0");Q40=makeQuery(id+"F0.imprint","IMPRINT",FACE,{"disambiguationData":[TD([[makeQuery(id+"F0.imprint","IMPRINT",EDGE,{"derivedFrom":subQ0}),1.0]])]});}
            var Q41;
            {var subQ0=sQuery(id+"F0.wireOp",EDGE,"E0.4");Q41=makeQuery(id+"F0.imprint","IMPRINT",FACE,{"disambiguationData":[TD([[makeQuery(id+"F0.imprint","IMPRINT",EDGE,{"derivedFrom":subQ0}),1.0]])]});}
            extrude(context, id + "F1", {"entities" : qUnion([Q0, Q1, Q2, Q3, Q4, Q5, Q6, Q7, Q8, Q9, Q10, Q11, Q12, Q13, Q14, Q15, Q16, Q17, Q18, Q19, Q20, Q21, Q22, Q23, Q24, Q25, Q26, Q27, Q28, Q29, Q30, Q31, Q32, Q33, Q34, Q35, Q36, Q37, Q38, Q39, Q40, Q41]), "depth" : 5 * mm, "offsetDistance" : 25 * mm});
        }
    });
